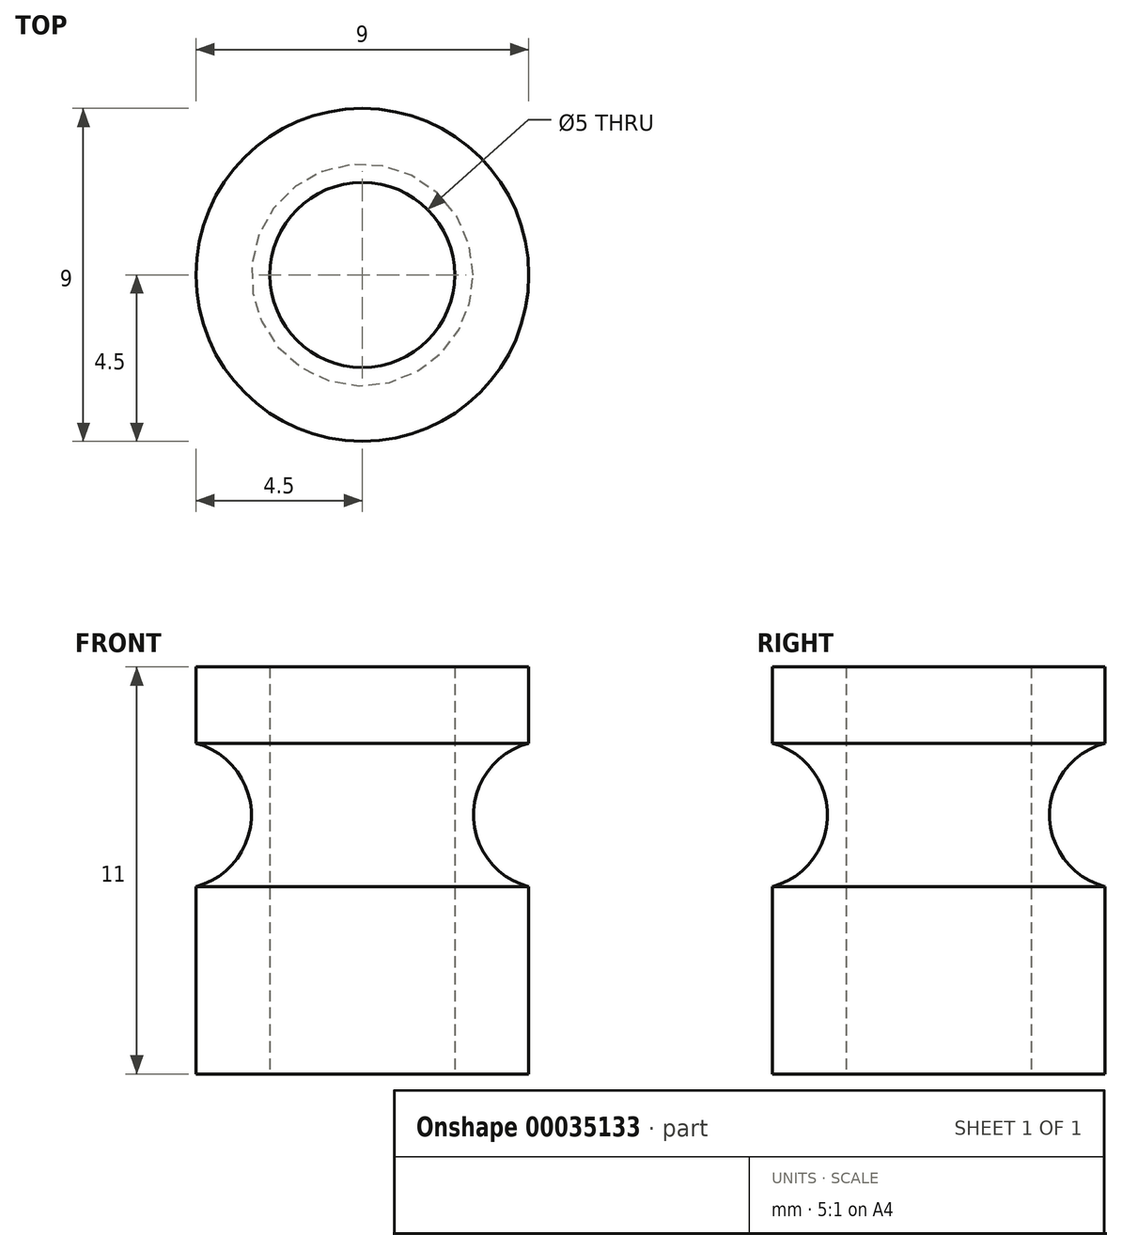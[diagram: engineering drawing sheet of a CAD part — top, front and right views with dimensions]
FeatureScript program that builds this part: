
annotation { "Feature Type Name" : "Feature", "Feature Type Description" : "" }
export const myFeature = defineFeature(function(context is Context, id is Id, definition is map)
    precondition{}
    {
        {
            assignVariable(context, id + "F0", {"name" : "MK8Length", "anyValue" : 11 * mm});
        }
        {
            var Q0;
            Q0=qCreatedBy(makeId("Top.planeOp"),FACE);
            var sketch = newSketch(context, id + "F1", { "sketchPlane" : qUnion([Q0])});
            skCircle(sketch, "E0", {"center": v(0, 0) * mm, "radius": 4.5 * mm});
            skCircle(sketch, "E1", {"center": v(0, 0) * mm, "radius": 2.5 * mm});
            skSolve(sketch);
        }
        {
            var Q0;
            Q0 = qSketchRegion(id + "F1", true);
            extrude(context, id + "F2", {"entities" : qUnion([Q0]), "depth" : getVariable(context, 'MK8Length')});
        }
        {
            var Q0;
            Q0=qCreatedBy(makeId("Front.planeOp"),FACE);
            var sketch = newSketch(context, id + "F3", { "sketchPlane" : qUnion([Q0])});
            skCircle(sketch, "E2", {"center": v(-5, 7) * mm, "radius": 2 * mm});
            skSolve(sketch);
        }
        {
            var Q0;
            Q0=makeQuery(id+"F3.imprint","IMPRINT",FACE,{"disambiguationData":[TD([[makeQuery(id+"F3.imprint","IMPRINT",EDGE,{"derivedFrom":sQuery(id+"F3.wireOp",EDGE,"E2")}),1.0]])]});
            var Q1;
            Q1=makeQuery(id+"F2.opExtrude","CAP_EDGE",EDGE,{"disambiguationData":[OSD([sQuery(id+"F1.wireOp",EDGE,"E0")])],"isStart":false});
            revolve(context, id + "F4", {"operationType" : NewBodyOperationType.REMOVE, "entities" : qUnion([Q0]), "axis" : qUnion([Q1]), "revolveType" : RevolveType.FULL, "oppositeDirection" : true});
        }
    });
